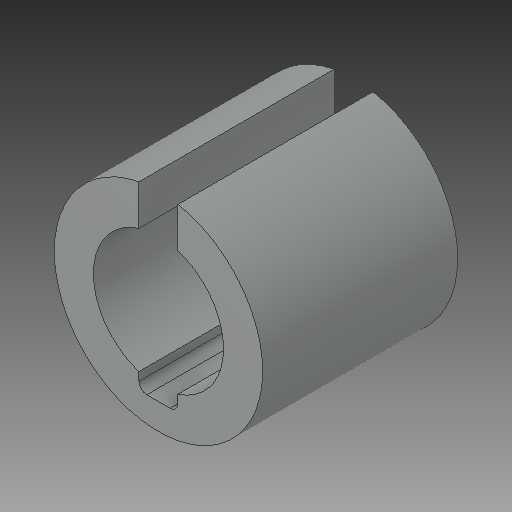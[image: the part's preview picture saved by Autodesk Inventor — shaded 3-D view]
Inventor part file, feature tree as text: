
AUTODESK INVENTOR PART (.ipt)
format: ipt  version: 2018 (Build 220112000, 112)  size: 115,712 bytes
history: native  units: in
note: dims shown in document units (in); Inventor stores cm internally (conversion verified against a paired STEP export)
features: fillet x1
ambient origin geometry x8: Origin, YZ Plane, XZ Plane, XY Plane, X Axis, Y Axis, Z Axis, Center Point
bodies: Solid1 (feature_tree)
feature tree (1):
  fillet  "Fillet1"  [1 undecoded]
note: 1 required parameter value undecoded (feature->parameter linkage not recoverable at this tier; creation-order binding heuristic only, values carry confidence <= 0.55)
